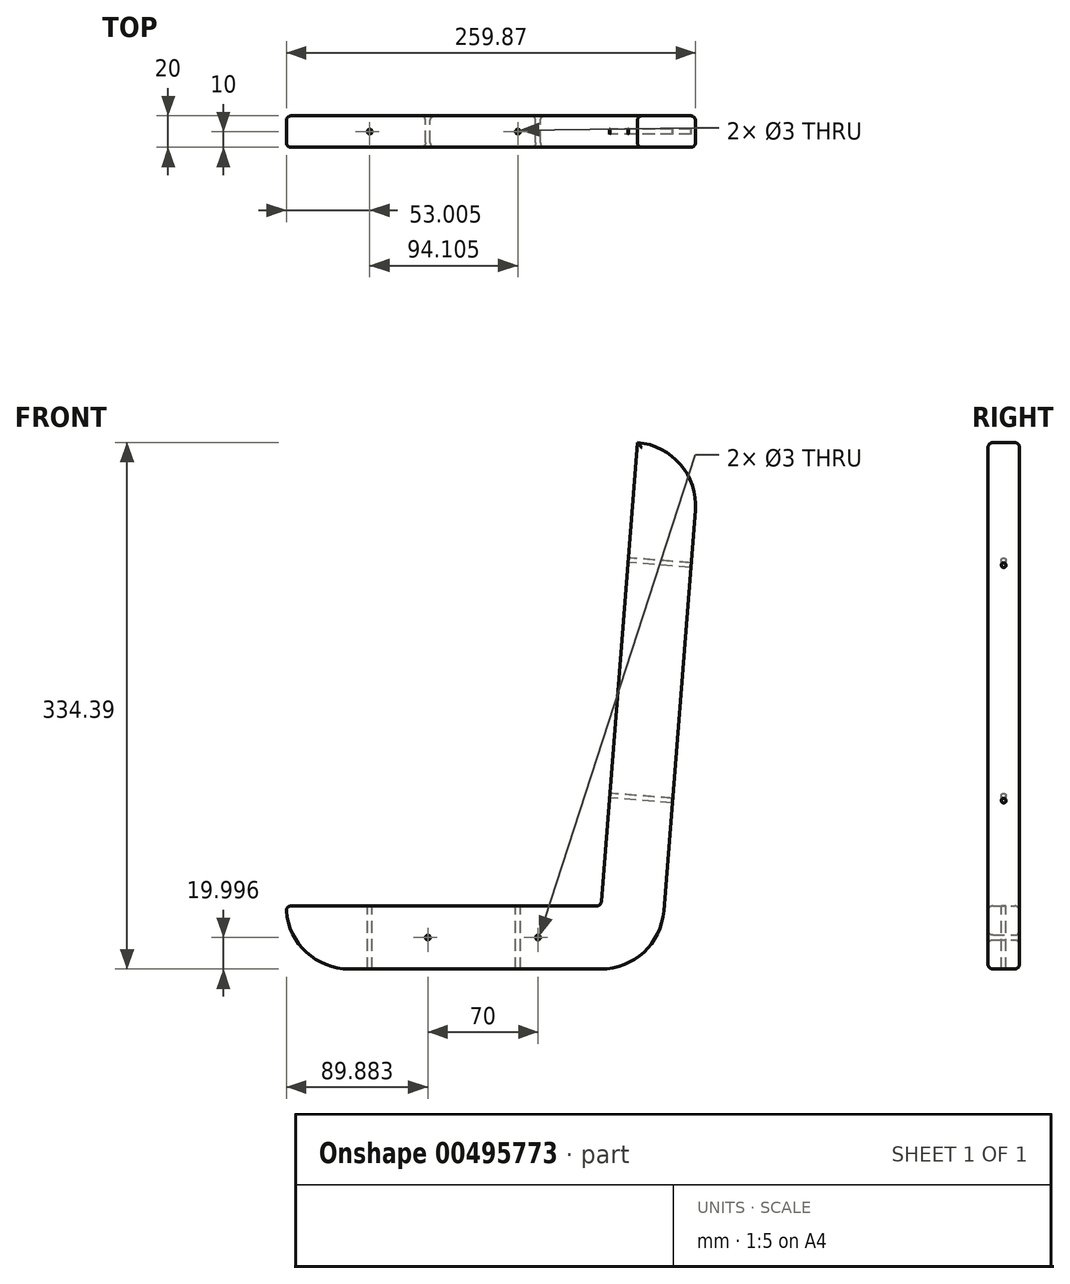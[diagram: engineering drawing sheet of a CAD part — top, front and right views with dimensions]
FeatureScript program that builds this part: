
annotation { "Feature Type Name" : "Feature", "Feature Type Description" : "" }
export const myFeature = defineFeature(function(context is Context, id is Id, definition is map)
    precondition{}
    {
        {
            var Q0;
            Q0=qCreatedBy(makeId("Front.planeOp"),FACE);
            var sketch = newSketch(context, id + "F0", { "sketchPlane" : qUnion([Q0])});
            skLineSegment(sketch, "E0", {"start": v(-117.93, -77.91) * mm, "end": v(-77.93, -77.91) * mm});
            skLineSegment(sketch, "E1", {"start": v(82.07, -77.91) * mm, "end": v(102.06, 176.6) * mm});
            skLineSegment(sketch, "E2.0", {"start": v(-77.93, -117.91) * mm, "end": v(82.07, -117.91) * mm});
            skLineSegment(sketch, "E3.0", {"start": v(121.95, -81.04) * mm, "end": v(141.93, 173.47) * mm});
            skArc(sketch, "E4", {"start": v(82.07, -117.91) * mm, "mid": v(109.23, -107.28) * mm, "end": v(121.95, -81.04) * mm});
            skLineSegment(sketch, "E5", {"start": v(102.06, 176.6) * mm, "end": v(105.19, 216.48) * mm});
            skLineSegment(sketch, "E6", {"start": v(-77.93, -77.91) * mm, "end": v(82.07, -77.91) * mm});
            skArc(sketch, "E7", {"start": v(105.19, 216.48) * mm, "mid": v(132.47, 202.59) * mm, "end": v(141.93, 173.47) * mm});
            skArc(sketch, "E8", {"start": v(-117.93, -77.91) * mm, "mid": v(-106.21, -106.2) * mm, "end": v(-77.93, -117.91) * mm});
            skPoint(sketch, "E9", {"position": v(-77.93, -97.91) * mm});
            skPoint(sketch, "E10.orphan", {"position": v(122, 175.04) * mm});
            skLineSegment(sketch, "E11", {"start": v(-27.93, -97.91) * mm, "end": v(42.07, -97.91) * mm});
            skPoint(sketch, "E12.end.orphan", {"position": v(112.07, -97.91) * mm});
            skCircle(sketch, "E13", {"center": v(-27.93, -97.91) * mm, "radius": 1.5 * mm});
            skCircle(sketch, "E14", {"center": v(42.07, -97.91) * mm, "radius": 1.5 * mm});
            skSolve(sketch);
        }
        {
            var Q0;
            Q0=makeQuery(id+"F0.imprint","IMPRINT",FACE,{"disambiguationData":[TD([[makeQuery(id+"F0.imprint","IMPRINT",EDGE,{"derivedFrom":sQuery(id+"F0.wireOp",EDGE,"E0")}),-1.0]])]});
            extrude(context, id + "F1", {"entities" : qUnion([Q0]), "endBound" : BoundingType.SYMMETRIC, "depth" : 20 * mm});
        }
        {
            var Q0;
            Q0=makeQuery(id+"F1.opExtrude","CAP_FACE",FACE,{"disambiguationData":[OSD([sQuery(id+"F0.wireOp",EDGE,"E0"),sQuery(id+"F0.wireOp",EDGE,"E1"),sQuery(id+"F0.wireOp",EDGE,"E2.0"),sQuery(id+"F0.wireOp",EDGE,"E3.0"),sQuery(id+"F0.wireOp",EDGE,"E4"),sQuery(id+"F0.wireOp",EDGE,"E5"),sQuery(id+"F0.wireOp",EDGE,"E6"),sQuery(id+"F0.wireOp",EDGE,"E7"),sQuery(id+"F0.wireOp",EDGE,"E8"),sQuery(id+"F0.wireOp",EDGE,"39GIcCKL-Pfxp-rZo1-XBFu-vlkC7OgBAQAQ"),sQuery(id+"F0.wireOp",EDGE,"py6rhHWJ-t2jt-od1s-v0KI-6Q1kR0UqvMmn"),sQuery(id+"F0.wireOp",EDGE,"E13"),sQuery(id+"F0.wireOp",EDGE,"E14")])],"isStart":false});
            var Q1;
            Q1=makeQuery(id+"F1.opExtrude","CAP_FACE",FACE,{"disambiguationData":[OSD([sQuery(id+"F0.wireOp",EDGE,"E0"),sQuery(id+"F0.wireOp",EDGE,"E1"),sQuery(id+"F0.wireOp",EDGE,"E2.0"),sQuery(id+"F0.wireOp",EDGE,"E3.0"),sQuery(id+"F0.wireOp",EDGE,"E4"),sQuery(id+"F0.wireOp",EDGE,"E5"),sQuery(id+"F0.wireOp",EDGE,"E6"),sQuery(id+"F0.wireOp",EDGE,"E7"),sQuery(id+"F0.wireOp",EDGE,"E8"),sQuery(id+"F0.wireOp",EDGE,"39GIcCKL-Pfxp-rZo1-XBFu-vlkC7OgBAQAQ"),sQuery(id+"F0.wireOp",EDGE,"py6rhHWJ-t2jt-od1s-v0KI-6Q1kR0UqvMmn"),sQuery(id+"F0.wireOp",EDGE,"E13"),sQuery(id+"F0.wireOp",EDGE,"E14")])],"isStart":true});
            var Q2;
            Q2=makeQuery(id+"F1.opExtrude","SWEPT_FACE",FACE,{"disambiguationData":[OSD([sQuery(id+"F0.wireOp",EDGE,"E0"),sQuery(id+"F0.wireOp",EDGE,"E6")])]});
            fillet(context, id + "F2", {"entities" : qUnion([Q0, Q1, Q2]), "radius" : 3 * mm, "tangentPropagation" : true, "allowEdgeOverflow" : false});
        }
        {
            var Q0;
            Q0=makeQuery(id+"F1.opExtrude","SWEPT_FACE",FACE,{"disambiguationData":[OSD([sQuery(id+"F0.wireOp",EDGE,"E0"),sQuery(id+"F0.wireOp",EDGE,"E6")])]});
            var sketch = newSketch(context, id + "F3", { "sketchPlane" : qUnion([Q0])});
            skLineSegment(sketch, "E15", {"start": v(-64.8, 0) * mm, "end": v(29.3, 0) * mm});
            skPoint(sketch, "E16.start.orphan", {"position": v(-114.8, 0) * mm});
            skPoint(sketch, "E17.end.orphan", {"position": v(79.3, 0) * mm});
            skSolve(sketch);
        }
        {
            var Q0;
            Q0=sQuery(id+"F3.wireOp",VERTEX,"E15.start");
            var Q1;
            Q1=makeQuery(id+"F1.opExtrude","SWEPT_BODY",BODY,{"disambiguationData":[OSD([sQuery(id+"F0.wireOp",EDGE,"E0"),sQuery(id+"F0.wireOp",EDGE,"E1"),sQuery(id+"F0.wireOp",EDGE,"E2.0"),sQuery(id+"F0.wireOp",EDGE,"E3.0"),sQuery(id+"F0.wireOp",EDGE,"E4"),sQuery(id+"F0.wireOp",EDGE,"E5"),sQuery(id+"F0.wireOp",EDGE,"E6"),sQuery(id+"F0.wireOp",EDGE,"E7"),sQuery(id+"F0.wireOp",EDGE,"E8"),sQuery(id+"F0.wireOp",EDGE,"39GIcCKL-Pfxp-rZo1-XBFu-vlkC7OgBAQAQ"),sQuery(id+"F0.wireOp",EDGE,"py6rhHWJ-t2jt-od1s-v0KI-6Q1kR0UqvMmn"),sQuery(id+"F0.wireOp",EDGE,"E13"),sQuery(id+"F0.wireOp",EDGE,"E14")])]});
            hole(context, id + "F4", {"style" : HoleStyle.SIMPLE, "endStyle" : HoleEndStyle.BLIND, "holeDiameter" : 3 * mm, "holeDepth" : 40 * mm, "isTappedThrough" : true, "tappedDepth" : 12 * mm, "tapClearance" : 3, "locations" : qUnion([Q0]), "scope" : qUnion([Q1])});
        }
        {
            var Q0;
            Q0=sQuery(id+"F3.wireOp",VERTEX,"E15.end");
            var Q1;
            Q1=makeQuery(id+"F1.opExtrude","SWEPT_BODY",BODY,{"disambiguationData":[OSD([sQuery(id+"F0.wireOp",EDGE,"E0"),sQuery(id+"F0.wireOp",EDGE,"E1"),sQuery(id+"F0.wireOp",EDGE,"E2.0"),sQuery(id+"F0.wireOp",EDGE,"E3.0"),sQuery(id+"F0.wireOp",EDGE,"E4"),sQuery(id+"F0.wireOp",EDGE,"E5"),sQuery(id+"F0.wireOp",EDGE,"E6"),sQuery(id+"F0.wireOp",EDGE,"E7"),sQuery(id+"F0.wireOp",EDGE,"E8"),sQuery(id+"F0.wireOp",EDGE,"39GIcCKL-Pfxp-rZo1-XBFu-vlkC7OgBAQAQ"),sQuery(id+"F0.wireOp",EDGE,"py6rhHWJ-t2jt-od1s-v0KI-6Q1kR0UqvMmn"),sQuery(id+"F0.wireOp",EDGE,"E13"),sQuery(id+"F0.wireOp",EDGE,"E14")])]});
            hole(context, id + "F5", {"style" : HoleStyle.SIMPLE, "endStyle" : HoleEndStyle.BLIND, "holeDiameter" : 3 * mm, "holeDepth" : 40 * mm, "isTappedThrough" : true, "tappedDepth" : 12 * mm, "tapClearance" : 3, "locations" : qUnion([Q0]), "scope" : qUnion([Q1])});
        }
        {
            var Q0;
            Q0=makeQuery(id+"F1.opExtrude","SWEPT_FACE",FACE,{"disambiguationData":[OSD([sQuery(id+"F0.wireOp",EDGE,"E1"),sQuery(id+"F0.wireOp",EDGE,"E5")])]});
            var sketch = newSketch(context, id + "F6", { "sketchPlane" : qUnion([Q0])});
            skLineSegment(sketch, "E18", {"start": v(0, 149.05) * mm, "end": v(0, -0.95) * mm});
            skPoint(sketch, "E19.start.orphan", {"position": v(0, 224.05) * mm});
            skLineSegment(sketch, "E20", {"start": v(0, 0) * mm, "end": v(0, -68.48) * mm});
            skSolve(sketch);
        }
        {
            var Q0;
            Q0=sQuery(id+"F6.wireOp",VERTEX,"E18.start");
            var Q1;
            Q1=sQuery(id+"F6.wireOp",VERTEX,"E18.end");
            var Q2;
            Q2=makeQuery(id+"F1.opExtrude","SWEPT_BODY",BODY,{"disambiguationData":[OSD([sQuery(id+"F0.wireOp",EDGE,"E0"),sQuery(id+"F0.wireOp",EDGE,"E1"),sQuery(id+"F0.wireOp",EDGE,"E2.0"),sQuery(id+"F0.wireOp",EDGE,"E3.0"),sQuery(id+"F0.wireOp",EDGE,"E4"),sQuery(id+"F0.wireOp",EDGE,"E5"),sQuery(id+"F0.wireOp",EDGE,"E6"),sQuery(id+"F0.wireOp",EDGE,"E7"),sQuery(id+"F0.wireOp",EDGE,"E8"),sQuery(id+"F0.wireOp",EDGE,"39GIcCKL-Pfxp-rZo1-XBFu-vlkC7OgBAQAQ"),sQuery(id+"F0.wireOp",EDGE,"py6rhHWJ-t2jt-od1s-v0KI-6Q1kR0UqvMmn"),sQuery(id+"F0.wireOp",EDGE,"E13"),sQuery(id+"F0.wireOp",EDGE,"E14")])]});
            hole(context, id + "F7", {"style" : HoleStyle.SIMPLE, "endStyle" : HoleEndStyle.BLIND, "holeDiameter" : 3 * mm, "holeDepth" : 40 * mm, "isTappedThrough" : true, "tappedDepth" : 12 * mm, "tapClearance" : 3, "locations" : qUnion([Q0, Q1]), "scope" : qUnion([Q2])});
        }
    });
